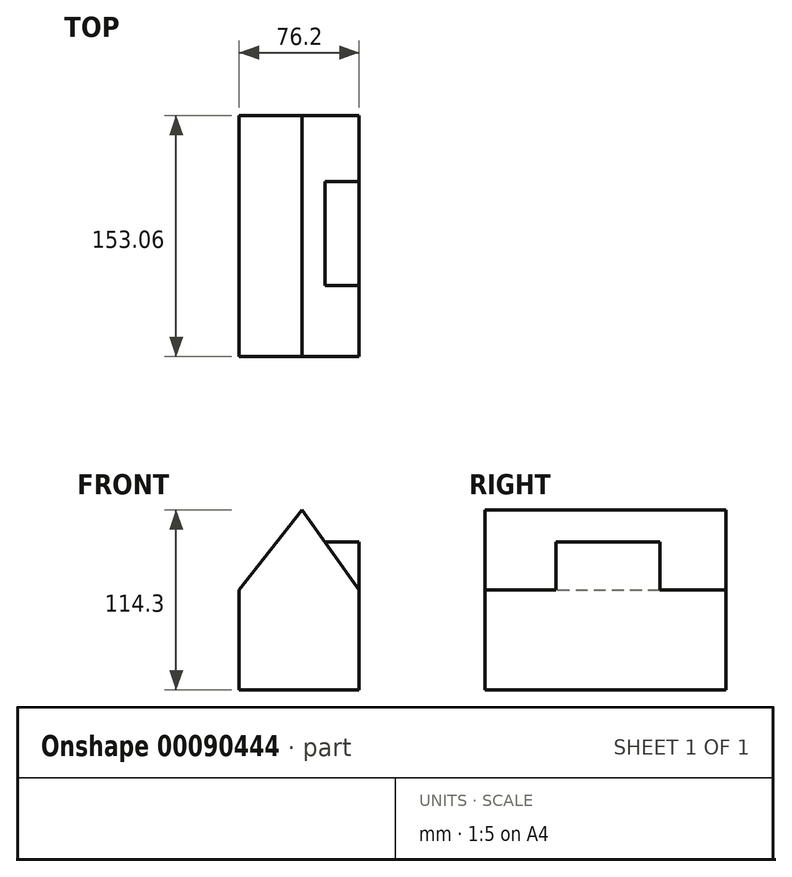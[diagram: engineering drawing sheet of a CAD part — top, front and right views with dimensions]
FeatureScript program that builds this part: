
annotation { "Feature Type Name" : "Feature", "Feature Type Description" : "" }
export const myFeature = defineFeature(function(context is Context, id is Id, definition is map)
    precondition{}
    {
        {
            var Q0;
            Q0=qCreatedBy(makeId("Front.planeOp"),FACE);
            var sketch = newSketch(context, id + "F0", { "sketchPlane" : qUnion([Q0])});
            skLineSegment(sketch, "E0.bottom", {"start": v(0, 0) * mm, "end": v(76.2, 0) * mm});
            skLineSegment(sketch, "E0.top", {"start": v(0, 63.5) * mm, "end": v(76.2, 63.5) * mm});
            skLineSegment(sketch, "E0.left", {"start": v(0, 0) * mm, "end": v(0, 63.5) * mm});
            skLineSegment(sketch, "E0.right", {"start": v(76.2, 0) * mm, "end": v(76.2, 63.5) * mm});
            skLineSegment(sketch, "E1", {"start": v(0, 63.5) * mm, "end": v(39.9, 114.3) * mm});
            skLineSegment(sketch, "E2", {"start": v(39.9, 114.3) * mm, "end": v(76.2, 63.5) * mm});
            skSolve(sketch);
        }
        {
            var Q0;
            Q0=makeQuery(id+"F0.imprint","IMPRINT",FACE,{"disambiguationData":[TD([[makeQuery(id+"F0.imprint","IMPRINT",EDGE,{"derivedFrom":sQuery(id+"F0.wireOp",EDGE,"E0.bottom")}),1.0]])]});
            var Q1;
            Q1=makeQuery(id+"F0.imprint","IMPRINT",FACE,{"disambiguationData":[TD([[makeQuery(id+"F0.imprint","IMPRINT",EDGE,{"derivedFrom":sQuery(id+"F0.wireOp",EDGE,"E0.top")}),1.0]])]});
            extrude(context, id + "F1", {"entities" : qUnion([Q0, Q1]), "depth" : 153.06 * mm});
        }
        {
            var Q0;
            Q0=makeQuery(id+"F1.opExtrude","SWEPT_FACE",FACE,{"disambiguationData":[OSD([sQuery(id+"F0.wireOp",EDGE,"E0.right")])]});
            var sketch = newSketch(context, id + "F2", { "sketchPlane" : qUnion([Q0])});
            skLineSegment(sketch, "E3.bottom", {"start": v(-108.04, 93.96) * mm, "end": v(-42.05, 93.96) * mm});
            skLineSegment(sketch, "E3.top", {"start": v(-108.04, 63.5) * mm, "end": v(-42.05, 63.5) * mm});
            skLineSegment(sketch, "E3.left", {"start": v(-108.04, 93.96) * mm, "end": v(-108.04, 63.5) * mm});
            skLineSegment(sketch, "E3.right", {"start": v(-42.05, 93.96) * mm, "end": v(-42.05, 63.5) * mm});
            skSolve(sketch);
        }
        {
            var Q0;
            Q0=makeQuery(id+"F2.imprint","IMPRINT",FACE,{"disambiguationData":[TD([[makeQuery(id+"F2.imprint","IMPRINT",EDGE,{"derivedFrom":sQuery(id+"F2.wireOp",EDGE,"E3.bottom")}),-1.0]])]});
            extrude(context, id + "F3", {"entities" : qUnion([Q0]), "operationType" : NewBodyOperationType.ADD, "oppositeDirection" : true, "depth" : 35.62 * mm});
        }
    });
